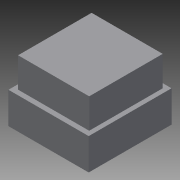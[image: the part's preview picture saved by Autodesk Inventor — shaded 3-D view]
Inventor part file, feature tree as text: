
AUTODESK INVENTOR PART (.ipt)
format: ipt  version: 2014 (Build 180170000, 170)  size: 81,920 bytes
history: native  units: in
note: dims shown in document units (in); Inventor stores cm internally (conversion verified against a paired STEP export)
features: extrude x2, sketch x2
ambient origin geometry x8: Origin, YZ Plane, XZ Plane, XY Plane, X Axis, Y Axis, Z Axis, Center Point
bodies: Solid1 (feature_tree)
feature tree (4):
  extrude  "Extrusion1"  Depth=2.148in
  extrude  "Extrusion2"  Depth=1.9039in
  sketch  "Sketch1"  dims[d0=2.2181in d1=2.148in]
  sketch  "Sketch2"  dims[d2=0.8425in d3=0.0in d4=1.9039in d5=1.9685in d6=0.1181in d7=0.1181in d8=0.7972in d9=0.0in]
